# Revit family: Domotics-DomesticRanges-GEWISS-27COMBI_SYSTEM-IP55_FIXING_POST_BRACKET
name_source: partatom
category: Apparecchi elettrici
revit_build: Autodesk Revit 2016 (Build: 20161004_0715(x64)
units: mm (PartAtom-declared; Revit-internal decimal feet)

## family parameters
Condiviso = No
Host = Superficie
Mantenere orientamento annotazione = No
Numero OmniClass = 23.80.30.14.24
Punto di calcolo locali = No
Quota connettore circolare = Usa diametro
Taglio con vuoti quando caricato = Sì
Tipo di parte = Normale
Titolo OmniClass = Junction Boxes

## types (1)
- Domotics-DomesticRanges-GEWISS-27COMBI_SYSTEM-IP55_FIXING_POST_BRACKET
    Catalogue = DOMOTICS
    Catalogue Range = 27COMBI
    Colour = Grey RAL 7035
    Description: = 3 gang
    Descrizione = 3 GANG WATERTIGHT ENCL.FOR POST FIXING
    Door colour: = Transparent
    Door type = With membrane
    EAN code = 8011564055438
    Electrocod = 0212
    Fixing = Post bracket
    For pole Ã˜ = 54-76MM
    Glow Wire Test = 650°C
    IDF = 2b74a3d1-c86b-4a0d-9461-8d5ed67e54bd
    IDT = 412df75b-c3fd-4420-9821-ba4985a7eb74
    IP degree = IP55
    Immagine tipo = GW27057.jpg
    Installation temperature = -25 +60 °C
    Insulation class = II
    Lid screws = Stainless steel
    Modello = GW27057
    No. SYSTEM modules = 3 gang
    No. knockouts holes Ã˜20 = 1
    No. open holes = 1
    Offset = 0 mm  [stored 0 ft]
    Outer dim. LxHxD (mm) = 122x164x85
    Produttore = GEWISS S.p.A.
    Prospetto di default = 1219 mm
    SEO = Enclosure
    Shock resistance = IK07
    Standard; = EN 60670-1
    Technical sheet = https://www.gewiss.com
    Thermo-pressure with ball = 70
    Torque screws tightening = 0,8NM
    Type of knockout holes = Removable with tool
    URL = https://www.gewiss.com
    Version file RFA = 19.4

note: source unit labels omitted for Thermo-pressure with ball — the stored unit's dimension contradicts the parameter name (converter mislabeling)

note: [stored X ft] marks values corroborated as IEEE doubles in the binary element streams (Revit-internal decimal feet)
